# Revit family: Door-Operator_Electric_Tormax_iMotion-TN-110-Control-Box
name_source: partatom
category: Specialty Equipment
units: mm (PartAtom-declared; Revit-internal decimal feet)

## family parameters
Always vertical = No
Classification Number = 23.30.40.11.34
Cut with Voids When Loaded = No
Enable Cutting in Views = No
Maintain Annotation Orientation = No
Part Type = Normal
Room Calculation Point = No
Round Connector Dimension = Use Diameter
Shared = No
Work Plane-Based = Yes

## types (1)
- as Specified
    Assembly Code = C1020410
    Available Options = as Specified
    Breaker Required = 15 A
    Construction Details = https://www.arcat.com
    Default Elevation = 0' - 0"
    Description = Tormax iMotion TN 110 Control Box
    Electrical_Amperage = 10 A
    Electrical_Frequency = 60 Hz
    Electrical_Number of Poles = 1
    Electrical_VA = 1200 VA
    Electrical_Voltage = 120 V
    Expected Lifespan (Years) = 0
    Green Building-LEED = https://www.arcat.com
    Keynote = 08 71 13
    Maintenance Schedule (Months) = 0
    Manufacturer = TORMAX USA Inc.
    Manufacturer Fax = 210-494-5930
    Manufacturer Website = http://www.tormaxusa.com
    Model = iMotion TN 110 Control Box
    Product Data = https://www.arcat.com
    Revision = R1_2018-04
    Sales Information = http://www.tormaxusa.com
    SpecWizard = https://www.arcat.com
    Specification = https://www.arcat.com
    URL = http://www.tormaxusa.com
    Unit Depth = 0' - 6 1/8"
    Unit Height = 0' - 11 7/8"
    Unit Width = 0' - 11 7/8"
    Warranty Duration (Years) = 0

## geometry (parser evidence)
native form markers: Sweep x2
no freeform markers — native parametric forms only
